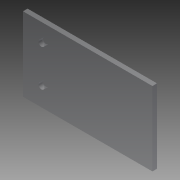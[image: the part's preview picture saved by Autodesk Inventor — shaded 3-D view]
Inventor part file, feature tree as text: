
AUTODESK INVENTOR PART (.ipt)
format: ipt  version: 2014 (Build 180170000, 170)  size: 78,336 bytes
history: native  units: in
note: dims shown in document units (in); Inventor stores cm internally (conversion verified against a paired STEP export)
features: extrude x1, sketch x1
ambient origin geometry x8: Origin, YZ Plane, XZ Plane, XY Plane, X Axis, Y Axis, Z Axis, Center Point
bodies: Solid1 (feature_tree)
feature tree (2):
  extrude  "Extrusion1"  Depth=3.5in
  sketch  "Sketch1"  dims[d0=2.0in d1=3.5in d2=0.163in d3=0.163in d4=0.5in d5=0.5in d6=1.0in d7=0.125in d8=0.0in]
